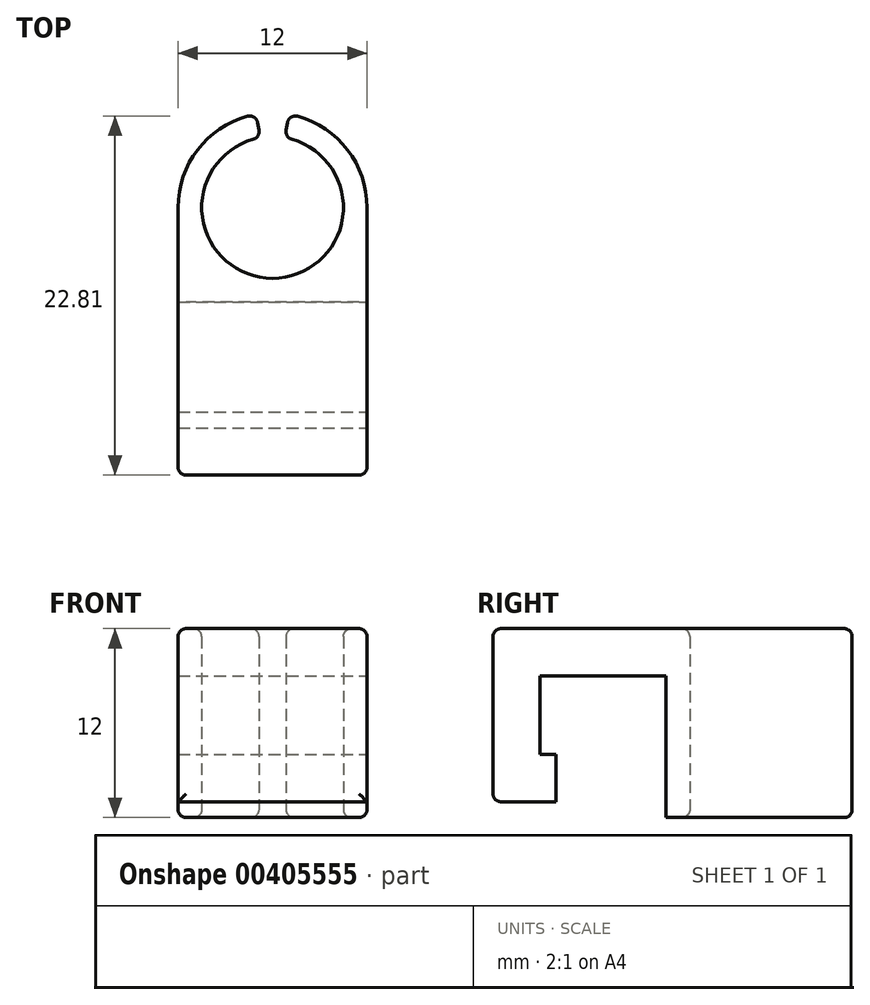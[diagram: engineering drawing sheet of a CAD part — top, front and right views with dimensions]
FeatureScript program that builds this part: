
annotation { "Feature Type Name" : "Feature", "Feature Type Description" : "" }
export const myFeature = defineFeature(function(context is Context, id is Id, definition is map)
    precondition{}
    {
        {
            var Q0;
            Q0=qCreatedBy(makeId("Top.planeOp"),FACE);
            var sketch = newSketch(context, id + "F0", { "sketchPlane" : qUnion([Q0])});
            skLineSegment(sketch, "E0.bottom", {"start": v(0, 0) * mm, "end": v(-12, 0) * mm});
            skLineSegment(sketch, "E0.top", {"start": v(0, 6) * mm, "end": v(-12, 6) * mm, "construction": true});
            skLineSegment(sketch, "E0.left", {"start": v(0, 0) * mm, "end": v(0, 6) * mm});
            skLineSegment(sketch, "E0.right", {"start": v(-12, 0) * mm, "end": v(-12, 6) * mm});
            skArc(sketch, "E1", {"start": v(0, 6) * mm, "mid": v(-1.4, 9.86) * mm, "end": v(-4.96, 11.9) * mm});
            skArc(sketch, "E2", {"start": v(-6.78, 10.43) * mm, "mid": v(-6, 1.5) * mm, "end": v(-5.22, 10.43) * mm});
            skArc(sketch, "E3", {"start": v(-7.04, 11.9) * mm, "mid": v(-10.6, 9.86) * mm, "end": v(-12, 6) * mm});
            skLineSegment(sketch, "E4", {"start": v(-6.78, 10.43) * mm, "end": v(-7.04, 11.9) * mm});
            skLineSegment(sketch, "E5", {"start": v(-5.22, 10.43) * mm, "end": v(-4.96, 11.9) * mm});
            skSolve(sketch);
        }
        {
            var Q0;
            Q0=makeQuery(id+"F0.imprint","IMPRINT",FACE,{"disambiguationData":[TD([[makeQuery(id+"F0.imprint","IMPRINT",EDGE,{"derivedFrom":sQuery(id+"F0.wireOp",EDGE,"E0.bottom")}),-1.0]])]});
            extrude(context, id + "F1", {"entities" : qUnion([Q0]), "depth" : 12 * mm});
        }
        {
            var Q0;
            Q0=makeQuery(id+"F1.opExtrude","SWEPT_EDGE",EDGE,{"disambiguationData":[OSD([sQuery(id+"F0.wireOp",EDGE,"E2"),sQuery(id+"F0.wireOp",EDGE,"E4")])]});
            var Q1;
            Q1=makeQuery(id+"F1.opExtrude","SWEPT_EDGE",EDGE,{"disambiguationData":[OSD([sQuery(id+"F0.wireOp",EDGE,"E3"),sQuery(id+"F0.wireOp",EDGE,"E4")])]});
            var Q2;
            Q2=makeQuery(id+"F1.opExtrude","SWEPT_EDGE",EDGE,{"disambiguationData":[OSD([sQuery(id+"F0.wireOp",EDGE,"E2"),sQuery(id+"F0.wireOp",EDGE,"E5")])]});
            var Q3;
            Q3=makeQuery(id+"F1.opExtrude","SWEPT_EDGE",EDGE,{"disambiguationData":[OSD([sQuery(id+"F0.wireOp",EDGE,"E1"),sQuery(id+"F0.wireOp",EDGE,"E5")])]});
            var Q4;
            Q4=makeQuery(id+"F1.opExtrude","CAP_EDGE",EDGE,{"disambiguationData":[OSD([sQuery(id+"F0.wireOp",EDGE,"E3")])],"isStart":true});
            var Q5;
            Q5=makeQuery(id+"F1.opExtrude","CAP_EDGE",EDGE,{"disambiguationData":[OSD([sQuery(id+"F0.wireOp",EDGE,"E3")])],"isStart":false});
            var Q6;
            Q6=makeQuery(id+"F1.opExtrude","CAP_EDGE",EDGE,{"disambiguationData":[OSD([sQuery(id+"F0.wireOp",EDGE,"E0.right")])],"isStart":true});
            var Q7;
            Q7=makeQuery(id+"F1.opExtrude","CAP_EDGE",EDGE,{"disambiguationData":[OSD([sQuery(id+"F0.wireOp",EDGE,"E0.right")])],"isStart":false});
            var Q8;
            Q8=makeQuery(id+"F1.opExtrude","CAP_EDGE",EDGE,{"disambiguationData":[OSD([sQuery(id+"F0.wireOp",EDGE,"E1")])],"isStart":true});
            var Q9;
            Q9=makeQuery(id+"F1.opExtrude","CAP_EDGE",EDGE,{"disambiguationData":[OSD([sQuery(id+"F0.wireOp",EDGE,"E0.left")])],"isStart":true});
            var Q10;
            Q10=makeQuery(id+"F1.opExtrude","CAP_EDGE",EDGE,{"disambiguationData":[OSD([sQuery(id+"F0.wireOp",EDGE,"E1")])],"isStart":false});
            var Q11;
            Q11=makeQuery(id+"F1.opExtrude","CAP_EDGE",EDGE,{"disambiguationData":[OSD([sQuery(id+"F0.wireOp",EDGE,"E0.left")])],"isStart":false});
            var Q12;
            Q12=makeQuery(id+"F1.opExtrude","CAP_EDGE",EDGE,{"disambiguationData":[OSD([sQuery(id+"F0.wireOp",EDGE,"E4")])],"isStart":true});
            var Q13;
            Q13=makeQuery(id+"F1.opExtrude","CAP_EDGE",EDGE,{"disambiguationData":[OSD([sQuery(id+"F0.wireOp",EDGE,"E5")])],"isStart":true});
            var Q14;
            Q14=makeQuery(id+"F1.opExtrude","CAP_EDGE",EDGE,{"disambiguationData":[OSD([sQuery(id+"F0.wireOp",EDGE,"E4")])],"isStart":false});
            var Q15;
            Q15=makeQuery(id+"F1.opExtrude","CAP_EDGE",EDGE,{"disambiguationData":[OSD([sQuery(id+"F0.wireOp",EDGE,"E5")])],"isStart":false});
            var Q16;
            Q16=makeQuery(id+"F1.opExtrude","CAP_EDGE",EDGE,{"disambiguationData":[OSD([sQuery(id+"F0.wireOp",EDGE,"E2")])],"isStart":false});
            var Q17;
            Q17=makeQuery(id+"F1.opExtrude","CAP_EDGE",EDGE,{"disambiguationData":[OSD([sQuery(id+"F0.wireOp",EDGE,"E2")])],"isStart":true});
            fillet(context, id + "F2", {"entities" : qUnion([Q0, Q1, Q2, Q3, Q4, Q5, Q6, Q7, Q8, Q9, Q10, Q11, Q12, Q13, Q14, Q15, Q16, Q17]), "radius" : 0.5 * mm, "tangentPropagation" : true, "allowEdgeOverflow" : false});
        }
        {
            var Q0;
            Q0=makeQuery(id+"F1.opExtrude","SWEPT_FACE",FACE,{"disambiguationData":[OSD([sQuery(id+"F0.wireOp",EDGE,"E0.left")])]});
            var sketch = newSketch(context, id + "F3", { "sketchPlane" : qUnion([Q0])});
            skLineSegment(sketch, "E6", {"start": v(0, 12) * mm, "end": v(-11, 12) * mm});
            skLineSegment(sketch, "E7", {"start": v(-11, 12) * mm, "end": v(-11, 1) * mm});
            skLineSegment(sketch, "E8", {"start": v(-8, 9) * mm, "end": v(0, 9) * mm});
            skLineSegment(sketch, "E9", {"start": v(0, 9) * mm, "end": v(0, 12) * mm});
            skLineSegment(sketch, "E10", {"start": v(-8, 9) * mm, "end": v(-8, 4) * mm});
            skLineSegment(sketch, "E11", {"start": v(-8, 4) * mm, "end": v(-7, 4) * mm});
            skLineSegment(sketch, "E12", {"start": v(-7, 4) * mm, "end": v(-7, 1) * mm});
            skLineSegment(sketch, "E13", {"start": v(-7, 1) * mm, "end": v(-11, 1) * mm});
            skSolve(sketch);
        }
        {
            var Q0;
            {var subQ3=sQuery(id+"F3.wireOp",EDGE,"E6");Q0=makeQuery(id+"F3.imprint","IMPRINT",FACE,{"disambiguationData":[TD([[makeQuery(id+"F3.imprint","IMPRINT",EDGE,{"derivedFrom":subQ3}),1.0]])]});}
            extrude(context, id + "F4", {"entities" : qUnion([Q0]), "operationType" : NewBodyOperationType.ADD, "oppositeDirection" : true, "depth" : 12 * mm});
        }
        {
            var Q0;
            Q0=makeQuery(id+"F4.opExtrude","CAP_EDGE",EDGE,{"disambiguationData":[OSD([sQuery(id+"F3.wireOp",EDGE,"E6")])],"isStart":true});
            var Q1;
            Q1=makeQuery(id+"F4.opExtrude","CAP_EDGE",EDGE,{"disambiguationData":[OSD([sQuery(id+"F3.wireOp",EDGE,"E6")])],"isStart":false});
            var Q2;
            Q2=makeQuery(id+"F4.opExtrude","CAP_EDGE",EDGE,{"disambiguationData":[OSD([sQuery(id+"F3.wireOp",EDGE,"E7")])],"isStart":false});
            var Q3;
            Q3=makeQuery(id+"F4.opExtrude","SWEPT_EDGE",EDGE,{"disambiguationData":[OSD([sQuery(id+"F3.wireOp",EDGE,"E6"),sQuery(id+"F3.wireOp",EDGE,"E7")])]});
            var Q4;
            Q4=makeQuery(id+"F4.opExtrude","CAP_EDGE",EDGE,{"disambiguationData":[OSD([sQuery(id+"F3.wireOp",EDGE,"E7")])],"isStart":true});
            var Q5;
            Q5=makeQuery(id+"F4.opExtrude","SWEPT_EDGE",EDGE,{"disambiguationData":[OSD([sQuery(id+"F3.wireOp",EDGE,"E7"),sQuery(id+"F3.wireOp",EDGE,"E13")])]});
            fillet(context, id + "F5", {"entities" : qUnion([Q0, Q1, Q2, Q3, Q4, Q5]), "radius" : 0.5 * mm, "tangentPropagation" : true, "allowEdgeOverflow" : false});
        }
    });
